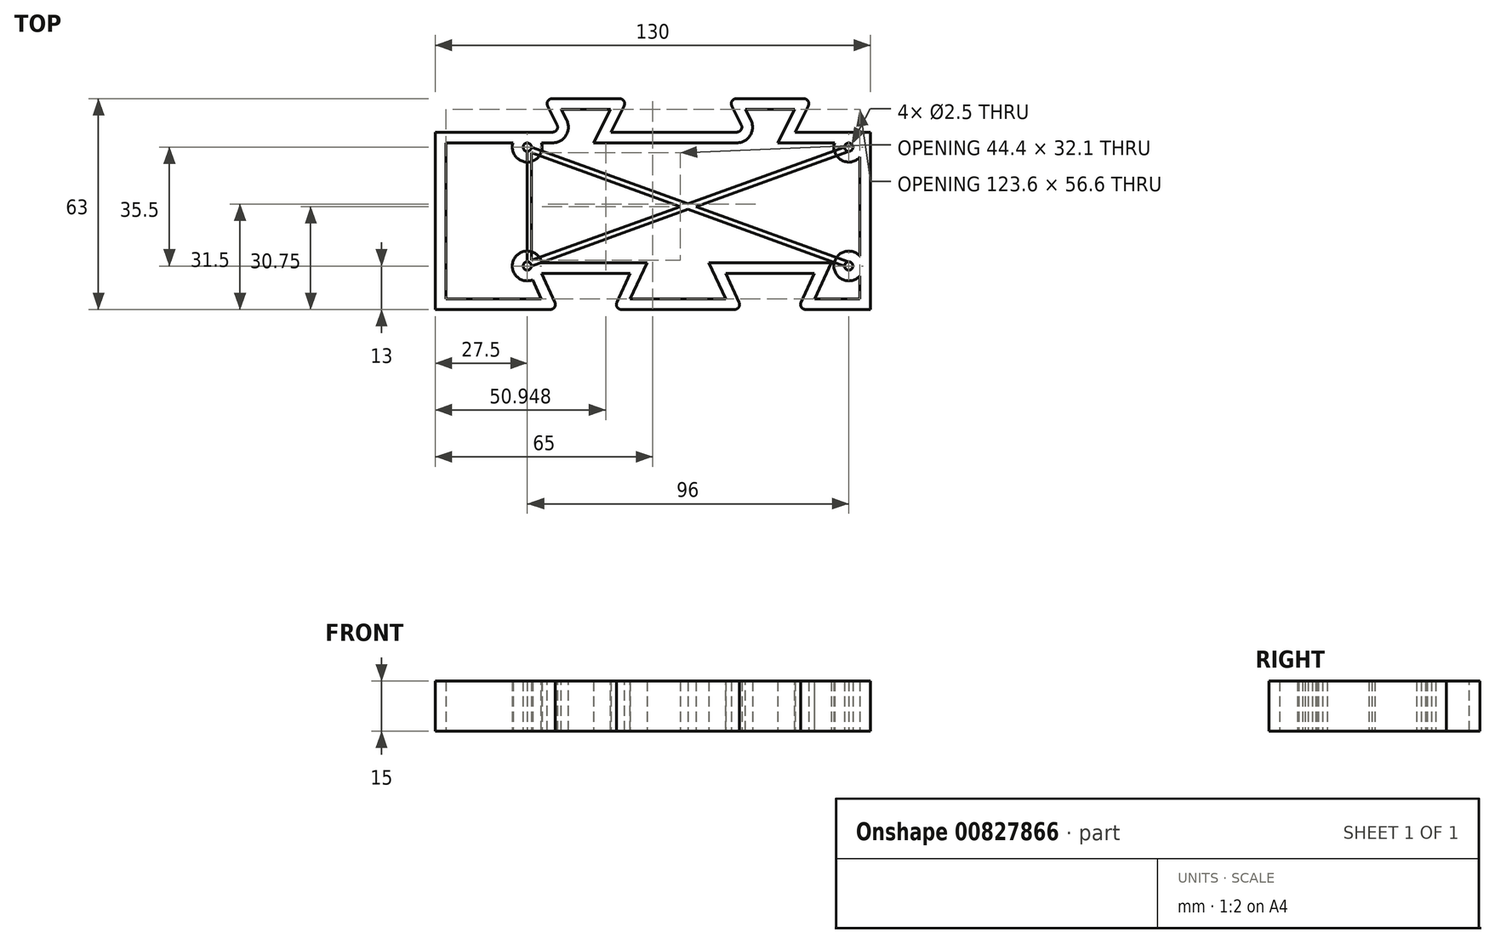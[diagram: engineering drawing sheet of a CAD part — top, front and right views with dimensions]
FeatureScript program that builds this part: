
annotation { "Feature Type Name" : "Feature", "Feature Type Description" : "" }
export const myFeature = defineFeature(function(context is Context, id is Id, definition is map)
    precondition{}
    {
        {
            var Q0;
            Q0=qCreatedBy(makeId("Top.planeOp"),FACE);
            var sketch = newSketch(context, id + "F0", { "sketchPlane" : qUnion([Q0])});
            skLineSegment(sketch, "E0.left", {"start": v(0, 0) * mm, "end": v(0, -53) * mm});
            skLineSegment(sketch, "E0.right", {"start": v(130, 0) * mm, "end": v(130, -53) * mm});
            skPoint(sketch, "E1", {"position": v(45, 0) * mm});
            skPoint(sketch, "E2", {"position": v(45, 10) * mm});
            skLineSegment(sketch, "E3", {"start": v(45, 10) * mm, "end": v(32.5, 10) * mm});
            skLineSegment(sketch, "E4", {"start": v(32.5, 10) * mm, "end": v(57.5, 10) * mm});
            skLineSegment(sketch, "E5", {"start": v(52.5, 0) * mm, "end": v(57.5, 10) * mm});
            skLineSegment(sketch, "E6", {"start": v(32.5, 10) * mm, "end": v(37.5, 0) * mm});
            skPoint(sketch, "E7", {"position": v(45, -53) * mm});
            skPoint(sketch, "E8", {"position": v(45, -42.25) * mm});
            skLineSegment(sketch, "E9", {"start": v(45, -42.25) * mm, "end": v(31.75, -42.25) * mm});
            skLineSegment(sketch, "E10", {"start": v(31.75, -42.25) * mm, "end": v(58.25, -42.25) * mm});
            skLineSegment(sketch, "E11", {"start": v(31.75, -42.25) * mm, "end": v(36.75, -53) * mm});
            skLineSegment(sketch, "E12", {"start": v(58.25, -42.25) * mm, "end": v(53.25, -53) * mm});
            skPoint(sketch, "E13", {"position": v(100, -53) * mm});
            skPoint(sketch, "E14", {"position": v(100, -42.25) * mm});
            skLineSegment(sketch, "E15", {"start": v(100, -42.25) * mm, "end": v(86.75, -42.25) * mm});
            skLineSegment(sketch, "E16", {"start": v(86.75, -42.25) * mm, "end": v(113.25, -42.25) * mm});
            skLineSegment(sketch, "E17", {"start": v(86.75, -42.25) * mm, "end": v(91.75, -53) * mm});
            skLineSegment(sketch, "E18", {"start": v(113.25, -42.25) * mm, "end": v(108.25, -53) * mm});
            skLineSegment(sketch, "E19", {"start": v(91.75, -53) * mm, "end": v(53.25, -53) * mm});
            skPoint(sketch, "E20", {"position": v(100, 0) * mm});
            skPoint(sketch, "E21", {"position": v(100, 10) * mm});
            skLineSegment(sketch, "E22", {"start": v(100, 10) * mm, "end": v(87.5, 10) * mm});
            skLineSegment(sketch, "E23", {"start": v(87.5, 10) * mm, "end": v(112.5, 10) * mm});
            skPoint(sketch, "E24", {"position": v(92.5, 0) * mm});
            skPoint(sketch, "E25", {"position": v(107.5, 0) * mm});
            skLineSegment(sketch, "E26", {"start": v(92.5, 0) * mm, "end": v(87.5, 10) * mm});
            skLineSegment(sketch, "E27", {"start": v(112.5, 10) * mm, "end": v(107.5, 0) * mm});
            skLineSegment(sketch, "E28", {"start": v(130, 0) * mm, "end": v(107.5, 0) * mm});
            skLineSegment(sketch, "E29", {"start": v(92.5, 0) * mm, "end": v(52.5, 0) * mm});
            skLineSegment(sketch, "E30", {"start": v(37.5, 0) * mm, "end": v(0, 0) * mm});
            skLineSegment(sketch, "E31", {"start": v(0, -53) * mm, "end": v(36.75, -53) * mm});
            skLineSegment(sketch, "E32", {"start": v(108.25, -53) * mm, "end": v(130, -53) * mm});
            skPoint(sketch, "E33", {"position": v(27.5, -40) * mm});
            skPoint(sketch, "E34", {"position": v(27.5, -4.5) * mm});
            skPoint(sketch, "E35", {"position": v(123.5, -4.5) * mm});
            skPoint(sketch, "E36", {"position": v(123.5, -40) * mm});
            skCircle(sketch, "E37", {"center": v(27.5, -4.5) * mm, "radius": 1.25 * mm});
            skCircle(sketch, "E38", {"center": v(123.5, -4.5) * mm, "radius": 1.25 * mm});
            skCircle(sketch, "E39", {"center": v(123.5, -40) * mm, "radius": 1.25 * mm});
            skCircle(sketch, "E40", {"center": v(27.5, -40) * mm, "radius": 1.25 * mm});
            skLineSegment(sketch, "E41", {"start": v(27.5, -5.75) * mm, "end": v(122.25, -40) * mm});
            skLineSegment(sketch, "E42", {"start": v(123.5, -38.75) * mm, "end": v(28.75, -4.5) * mm});
            skLineSegment(sketch, "E43", {"start": v(122.25, -4.5) * mm, "end": v(27.5, -38.75) * mm});
            skLineSegment(sketch, "E44", {"start": v(28.75, -40) * mm, "end": v(123.5, -5.75) * mm});
            skLineSegment(sketch, "E45", {"start": v(28.75, -4.5) * mm, "end": v(27.5, -5.75) * mm});
            skLineSegment(sketch, "E46", {"start": v(123.5, -38.75) * mm, "end": v(122.25, -40) * mm});
            skLineSegment(sketch, "E47", {"start": v(122.25, -4.5) * mm, "end": v(123.5, -5.75) * mm});
            skLineSegment(sketch, "E48", {"start": v(27.5, -38.75) * mm, "end": v(28.75, -40) * mm});
            skLineSegment(sketch, "E49", {"start": v(28.75, -6.2) * mm, "end": v(28.75, -38.3) * mm});
            skLineSegment(sketch, "E50", {"start": v(27.5, -38.75) * mm, "end": v(27.5, -5.75) * mm});
            skSolve(sketch);
        }
        {
            var Q0;
            Q0=makeQuery(id+"F0.imprint","IMPRINT",FACE,{"disambiguationData":[TD([[makeQuery(id+"F0.imprint","IMPRINT",EDGE,{"derivedFrom":sQuery(id+"F0.wireOp",EDGE,"E0.left")}),1.0]])]});
            var Q1;
            {var subQ1=sQuery(id+"F0.wireOp",EDGE,"E41");var subQ6=sQuery(id+"F0.wireOp",EDGE,"E43");var subQ7=makeQuery(id+"F0.imprint","INTERSECT",VERTEX,{"derivedFrom":[subQ1,subQ6]});Q1=makeQuery(id+"F0.imprint","IMPRINT",FACE,{"disambiguationData":[TD([[makeQuery(id+"F0.imprint","IMPRINT",EDGE,{"disambiguationData":[TD([[subQ7,1.0]])],"derivedFrom":subQ6}),-1.0]])]});}
            var Q2;
            {var subQ1=sQuery(id+"F0.wireOp",EDGE,"E43");var subQ6=sQuery(id+"F0.wireOp",EDGE,"E41");var subQ7=makeQuery(id+"F0.imprint","INTERSECT",VERTEX,{"derivedFrom":[subQ6,subQ1]});Q2=makeQuery(id+"F0.imprint","IMPRINT",FACE,{"disambiguationData":[TD([[makeQuery(id+"F0.imprint","IMPRINT",EDGE,{"disambiguationData":[TD([[subQ7,-1.0]])],"derivedFrom":subQ6}),-1.0]])]});}
            var Q3;
            {var subQ1=sQuery(id+"F0.wireOp",EDGE,"E41");var subQ6=sQuery(id+"F0.wireOp",EDGE,"E44");var subQ7=makeQuery(id+"F0.imprint","INTERSECT",VERTEX,{"derivedFrom":[subQ1,subQ6]});Q3=makeQuery(id+"F0.imprint","IMPRINT",FACE,{"disambiguationData":[TD([[makeQuery(id+"F0.imprint","IMPRINT",EDGE,{"disambiguationData":[TD([[subQ7,-1.0]])],"derivedFrom":subQ6}),-1.0]])]});}
            var Q4;
            {var subQ4=sQuery(id+"F0.wireOp",EDGE,"E44");var subQ6=sQuery(id+"F0.wireOp",EDGE,"E42");var subQ7=makeQuery(id+"F0.imprint","INTERSECT",VERTEX,{"derivedFrom":[subQ6,subQ4]});Q4=makeQuery(id+"F0.imprint","IMPRINT",FACE,{"disambiguationData":[TD([[makeQuery(id+"F0.imprint","IMPRINT",EDGE,{"disambiguationData":[TD([[subQ7,-1.0]])],"derivedFrom":subQ6}),-1.0]])]});}
            var Q5;
            {var subQ0=sQuery(id+"F0.wireOp",EDGE,"E43");var subQ1=sQuery(id+"F0.wireOp",EDGE,"E41");var subQ2=makeQuery(id+"F0.imprint","INTERSECT",VERTEX,{"derivedFrom":[subQ1,subQ0]});Q5=makeQuery(id+"F0.imprint","IMPRINT",FACE,{"disambiguationData":[TD([[makeQuery(id+"F0.imprint","IMPRINT",EDGE,{"disambiguationData":[TD([[subQ2,-1.0]])],"derivedFrom":subQ1}),1.0]])]});}
            var Q6;
            {var subQ2=sQuery(id+"F0.wireOp",EDGE,"E49");Q6=makeQuery(id+"F0.imprint","IMPRINT",FACE,{"disambiguationData":[TD([[makeQuery(id+"F0.imprint","IMPRINT",EDGE,{"derivedFrom":subQ2}),-1.0]])]});}
            var Q7;
            {var subQ0=sQuery(id+"F0.wireOp",EDGE,"E49");Q7=makeQuery(id+"F0.imprint","IMPRINT",FACE,{"disambiguationData":[TD([[makeQuery(id+"F0.imprint","IMPRINT",EDGE,{"derivedFrom":subQ0}),1.0]])]});}
            extrude(context, id + "F1", {"entities" : qUnion([Q0, Q1, Q2, Q3, Q4, Q5, Q6, Q7]), "depth" : 15 * mm, "offsetDistance" : 25 * mm});
        }
        {
            var Q0;
            Q0=makeQuery(id+"F1.opExtrude","SWEPT_EDGE",EDGE,{"disambiguationData":[OSD([sQuery(id+"F0.wireOp",EDGE,"E12"),sQuery(id+"F0.wireOp",EDGE,"E19")])]});
            var Q1;
            Q1=makeQuery(id+"F1.opExtrude","SWEPT_EDGE",EDGE,{"disambiguationData":[OSD([sQuery(id+"F0.wireOp",EDGE,"E18"),sQuery(id+"F0.wireOp",EDGE,"E32")])]});
            var Q2;
            Q2=makeQuery(id+"F1.opExtrude","SWEPT_EDGE",EDGE,{"disambiguationData":[OSD([sQuery(id+"F0.wireOp",EDGE,"E17"),sQuery(id+"F0.wireOp",EDGE,"E19")])]});
            var Q3;
            Q3=makeQuery(id+"F1.opExtrude","SWEPT_EDGE",EDGE,{"disambiguationData":[OSD([sQuery(id+"F0.wireOp",EDGE,"E4"),sQuery(id+"F0.wireOp",EDGE,"E6")])]});
            var Q4;
            Q4=makeQuery(id+"F1.opExtrude","SWEPT_EDGE",EDGE,{"disambiguationData":[OSD([sQuery(id+"F0.wireOp",EDGE,"E23"),sQuery(id+"F0.wireOp",EDGE,"E27")])]});
            var Q5;
            Q5=makeQuery(id+"F1.opExtrude","SWEPT_EDGE",EDGE,{"disambiguationData":[OSD([sQuery(id+"F0.wireOp",EDGE,"E4"),sQuery(id+"F0.wireOp",EDGE,"E5")])]});
            var Q6;
            Q6=makeQuery(id+"F1.opExtrude","SWEPT_EDGE",EDGE,{"disambiguationData":[OSD([sQuery(id+"F0.wireOp",EDGE,"E23"),sQuery(id+"F0.wireOp",EDGE,"E26")])]});
            var Q7;
            Q7=makeQuery(id+"F1.opExtrude","SWEPT_EDGE",EDGE,{"disambiguationData":[OSD([sQuery(id+"F0.wireOp",EDGE,"E11"),sQuery(id+"F0.wireOp",EDGE,"E31")])]});
            fillet(context, id + "F2", {"entities" : qUnion([Q0, Q1, Q2, Q3, Q4, Q5, Q6, Q7]), "radius" : 1.5 * mm, "tangentPropagation" : true, "allowEdgeOverflow" : false});
        }
        {
            var Q0;
            Q0=makeQuery(id+"F1.opExtrude","CAP_FACE",FACE,{"disambiguationData":[OSD([sQuery(id+"F0.wireOp",EDGE,"E0.left"),sQuery(id+"F0.wireOp",EDGE,"E0.right"),sQuery(id+"F0.wireOp",EDGE,"E4"),sQuery(id+"F0.wireOp",EDGE,"E5"),sQuery(id+"F0.wireOp",EDGE,"E6"),sQuery(id+"F0.wireOp",EDGE,"E10"),sQuery(id+"F0.wireOp",EDGE,"E11"),sQuery(id+"F0.wireOp",EDGE,"E12"),sQuery(id+"F0.wireOp",EDGE,"E16"),sQuery(id+"F0.wireOp",EDGE,"E17"),sQuery(id+"F0.wireOp",EDGE,"E18"),sQuery(id+"F0.wireOp",EDGE,"E19"),sQuery(id+"F0.wireOp",EDGE,"E23"),sQuery(id+"F0.wireOp",EDGE,"E26"),sQuery(id+"F0.wireOp",EDGE,"E27"),sQuery(id+"F0.wireOp",EDGE,"E28"),sQuery(id+"F0.wireOp",EDGE,"E29"),sQuery(id+"F0.wireOp",EDGE,"E30"),sQuery(id+"F0.wireOp",EDGE,"E31"),sQuery(id+"F0.wireOp",EDGE,"E32"),sQuery(id+"F0.wireOp",EDGE,"E37"),sQuery(id+"F0.wireOp",EDGE,"E38"),sQuery(id+"F0.wireOp",EDGE,"E39"),sQuery(id+"F0.wireOp",EDGE,"E40"),sQuery(id+"F0.wireOp",EDGE,"XoaqiCgA-ocFq-Pimf-wrHk-WjpAoFNvgXmC.bottom"),sQuery(id+"F0.wireOp",EDGE,"XoaqiCgA-ocFq-Pimf-wrHk-WjpAoFNvgXmC.top"),sQuery(id+"F0.wireOp",EDGE,"XoaqiCgA-ocFq-Pimf-wrHk-WjpAoFNvgXmC.left"),sQuery(id+"F0.wireOp",EDGE,"XoaqiCgA-ocFq-Pimf-wrHk-WjpAoFNvgXmC.right")])],"isStart":false});
            var Q1;
            Q1=makeQuery(id+"F1.opExtrude","CAP_FACE",FACE,{"disambiguationData":[OSD([sQuery(id+"F0.wireOp",EDGE,"E0.left"),sQuery(id+"F0.wireOp",EDGE,"E0.right"),sQuery(id+"F0.wireOp",EDGE,"E4"),sQuery(id+"F0.wireOp",EDGE,"E5"),sQuery(id+"F0.wireOp",EDGE,"E6"),sQuery(id+"F0.wireOp",EDGE,"E10"),sQuery(id+"F0.wireOp",EDGE,"E11"),sQuery(id+"F0.wireOp",EDGE,"E12"),sQuery(id+"F0.wireOp",EDGE,"E16"),sQuery(id+"F0.wireOp",EDGE,"E17"),sQuery(id+"F0.wireOp",EDGE,"E18"),sQuery(id+"F0.wireOp",EDGE,"E19"),sQuery(id+"F0.wireOp",EDGE,"E23"),sQuery(id+"F0.wireOp",EDGE,"E26"),sQuery(id+"F0.wireOp",EDGE,"E27"),sQuery(id+"F0.wireOp",EDGE,"E28"),sQuery(id+"F0.wireOp",EDGE,"E29"),sQuery(id+"F0.wireOp",EDGE,"E30"),sQuery(id+"F0.wireOp",EDGE,"E31"),sQuery(id+"F0.wireOp",EDGE,"E32"),sQuery(id+"F0.wireOp",EDGE,"E37"),sQuery(id+"F0.wireOp",EDGE,"E38"),sQuery(id+"F0.wireOp",EDGE,"E39"),sQuery(id+"F0.wireOp",EDGE,"E40"),sQuery(id+"F0.wireOp",EDGE,"XoaqiCgA-ocFq-Pimf-wrHk-WjpAoFNvgXmC.bottom"),sQuery(id+"F0.wireOp",EDGE,"XoaqiCgA-ocFq-Pimf-wrHk-WjpAoFNvgXmC.top"),sQuery(id+"F0.wireOp",EDGE,"XoaqiCgA-ocFq-Pimf-wrHk-WjpAoFNvgXmC.left"),sQuery(id+"F0.wireOp",EDGE,"XoaqiCgA-ocFq-Pimf-wrHk-WjpAoFNvgXmC.right")])],"isStart":true});
            shell(context, id + "F3", {"entities" : qUnion([Q0, Q1]), "thickness" : 3.2 * mm});
        }
        {
            var Q0;
            {var subQ1=sQuery(id+"F0.wireOp",EDGE,"E43");var subQ6=sQuery(id+"F0.wireOp",EDGE,"E41");var subQ7=makeQuery(id+"F0.imprint","INTERSECT",VERTEX,{"derivedFrom":[subQ6,subQ1]});Q0=makeQuery(id+"F0.imprint","IMPRINT",FACE,{"disambiguationData":[TD([[makeQuery(id+"F0.imprint","IMPRINT",EDGE,{"disambiguationData":[TD([[subQ7,-1.0]])],"derivedFrom":subQ6}),-1.0]])]});}
            var Q1;
            {var subQ1=sQuery(id+"F0.wireOp",EDGE,"E41");var subQ6=sQuery(id+"F0.wireOp",EDGE,"E43");var subQ7=makeQuery(id+"F0.imprint","INTERSECT",VERTEX,{"derivedFrom":[subQ1,subQ6]});Q1=makeQuery(id+"F0.imprint","IMPRINT",FACE,{"disambiguationData":[TD([[makeQuery(id+"F0.imprint","IMPRINT",EDGE,{"disambiguationData":[TD([[subQ7,1.0]])],"derivedFrom":subQ6}),-1.0]])]});}
            var Q2;
            {var subQ0=sQuery(id+"F0.wireOp",EDGE,"E43");var subQ1=sQuery(id+"F0.wireOp",EDGE,"E41");var subQ2=makeQuery(id+"F0.imprint","INTERSECT",VERTEX,{"derivedFrom":[subQ1,subQ0]});Q2=makeQuery(id+"F0.imprint","IMPRINT",FACE,{"disambiguationData":[TD([[makeQuery(id+"F0.imprint","IMPRINT",EDGE,{"disambiguationData":[TD([[subQ2,-1.0]])],"derivedFrom":subQ1}),1.0]])]});}
            var Q3;
            {var subQ4=sQuery(id+"F0.wireOp",EDGE,"E44");var subQ6=sQuery(id+"F0.wireOp",EDGE,"E42");var subQ7=makeQuery(id+"F0.imprint","INTERSECT",VERTEX,{"derivedFrom":[subQ6,subQ4]});Q3=makeQuery(id+"F0.imprint","IMPRINT",FACE,{"disambiguationData":[TD([[makeQuery(id+"F0.imprint","IMPRINT",EDGE,{"disambiguationData":[TD([[subQ7,-1.0]])],"derivedFrom":subQ6}),-1.0]])]});}
            var Q4;
            {var subQ1=sQuery(id+"F0.wireOp",EDGE,"E41");var subQ6=sQuery(id+"F0.wireOp",EDGE,"E44");var subQ7=makeQuery(id+"F0.imprint","INTERSECT",VERTEX,{"derivedFrom":[subQ1,subQ6]});Q4=makeQuery(id+"F0.imprint","IMPRINT",FACE,{"disambiguationData":[TD([[makeQuery(id+"F0.imprint","IMPRINT",EDGE,{"disambiguationData":[TD([[subQ7,-1.0]])],"derivedFrom":subQ6}),-1.0]])]});}
            var Q5;
            {var subQ2=sQuery(id+"F0.wireOp",EDGE,"E49");Q5=makeQuery(id+"F0.imprint","IMPRINT",FACE,{"disambiguationData":[TD([[makeQuery(id+"F0.imprint","IMPRINT",EDGE,{"derivedFrom":subQ2}),-1.0]])]});}
            var Q6;
            Q6=sQuery(id+"F0.wireOp",EDGE,"E41");
            var Q7;
            Q7=sQuery(id+"F0.wireOp",EDGE,"E42");
            var Q8;
            Q8=sQuery(id+"F0.wireOp",EDGE,"E44");
            var Q9;
            Q9=sQuery(id+"F0.wireOp",EDGE,"E43");
            extrude(context, id + "F4", {"entities" : qUnion([Q0, Q1, Q2, Q3, Q4, Q5]), "surfaceEntities" : qUnion([Q6, Q7, Q8, Q9]), "depth" : 15 * mm, "offsetDistance" : 25 * mm});
        }
    });
